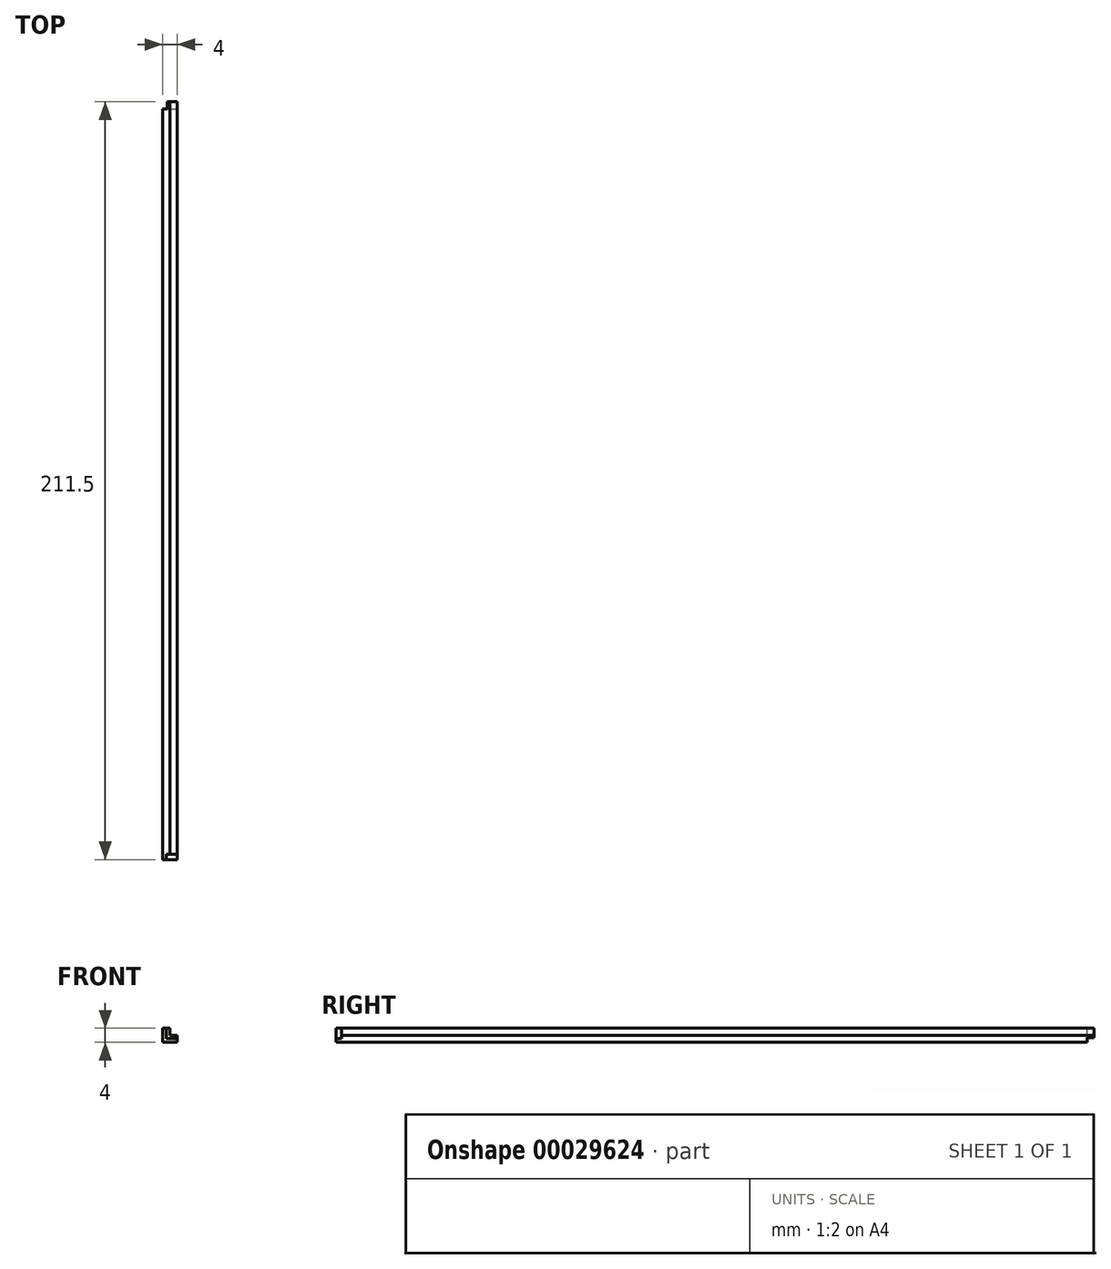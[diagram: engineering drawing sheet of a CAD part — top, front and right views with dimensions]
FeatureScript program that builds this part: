
annotation { "Feature Type Name" : "Feature", "Feature Type Description" : "" }
export const myFeature = defineFeature(function(context is Context, id is Id, definition is map)
    precondition{}
    {
        {
            var Q0;
            Q0=qCreatedBy(makeId("Top.planeOp"),FACE);
            var sketch = newSketch(context, id + "F0", { "sketchPlane" : qUnion([Q0])});
            skLineSegment(sketch, "E0.bottom", {"start": v(12.95, -61.2) * mm, "end": v(16.95, -61.2) * mm});
            skLineSegment(sketch, "E0.top", {"start": v(12.95, 148.8) * mm, "end": v(16.95, 148.8) * mm});
            skLineSegment(sketch, "E0.left", {"start": v(12.95, -61.2) * mm, "end": v(12.95, 148.8) * mm});
            skLineSegment(sketch, "E0.right", {"start": v(16.95, -61.2) * mm, "end": v(16.95, 148.8) * mm});
            skSolve(sketch);
        }
        {
            var Q0;
            Q0=makeQuery(id+"F0.imprint","IMPRINT",FACE,{"disambiguationData":[TD([[makeQuery(id+"F0.imprint","IMPRINT",EDGE,{"derivedFrom":sQuery(id+"F0.wireOp",EDGE,"E0.bottom")}),1.0]])]});
            extrude(context, id + "F1", {"entities" : qUnion([Q0]), "depth" : 2 * mm});
        }
        {
            var Q0;
            Q0=makeQuery(id+"F1.opExtrude","CAP_FACE",FACE,{"disambiguationData":[OSD([sQuery(id+"F0.wireOp",EDGE,"E0.bottom"),sQuery(id+"F0.wireOp",EDGE,"E0.top"),sQuery(id+"F0.wireOp",EDGE,"E0.left"),sQuery(id+"F0.wireOp",EDGE,"E0.right")])],"isStart":false});
            var sketch = newSketch(context, id + "F2", { "sketchPlane" : qUnion([Q0])});
            skLineSegment(sketch, "E1.bottom", {"start": v(12.95, -61.2) * mm, "end": v(14.95, -61.2) * mm});
            skLineSegment(sketch, "E1.left", {"start": v(12.95, -61.2) * mm, "end": v(12.95, 148.8) * mm});
            skLineSegment(sketch, "E2", {"start": v(14.95, -61.2) * mm, "end": v(14.95, 148.8) * mm});
            skLineSegment(sketch, "E3", {"start": v(14.95, 148.8) * mm, "end": v(12.95, 148.8) * mm});
            skSolve(sketch);
        }
        {
            var Q0;
            Q0=makeQuery(id+"F2.imprint","IMPRINT",FACE,{"disambiguationData":[TD([[makeQuery(id+"F2.imprint","IMPRINT",EDGE,{"derivedFrom":sQuery(id+"F2.wireOp",EDGE,"E1.bottom")}),1.0]])]});
            extrude(context, id + "F3", {"entities" : qUnion([Q0]), "operationType" : NewBodyOperationType.ADD, "depth" : 2 * mm});
        }
        {
            var Q0;
            Q0=makeQuery(id+"F3.boolean.opBoolean","MERGE",FACE,{"derivedFrom":[makeQuery(id+"F1.opExtrude","SWEPT_FACE",FACE,{"disambiguationData":[OSD([sQuery(id+"F0.wireOp",EDGE,"E0.top")])]}),makeQuery(id+"F3.opExtrude","SWEPT_FACE",FACE,{"disambiguationData":[OSD([sQuery(id+"F2.wireOp",EDGE,"E3")])]})]});
            var sketch = newSketch(context, id + "F4", { "sketchPlane" : qUnion([Q0])});
            skLineSegment(sketch, "E4", {"start": v(-12.95, 4) * mm, "end": v(-12.95, 0) * mm});
            skLineSegment(sketch, "E5", {"start": v(-12.95, 0) * mm, "end": v(-16.95, 0) * mm});
            skLineSegment(sketch, "E6", {"start": v(-16.95, 0) * mm, "end": v(-16.95, 1.3) * mm});
            skLineSegment(sketch, "E7", {"start": v(-14.25, 1.3) * mm, "end": v(-14.25, 4) * mm});
            skLineSegment(sketch, "E8", {"start": v(-14.25, 4) * mm, "end": v(-12.95, 4) * mm});
            skLineSegment(sketch, "E9", {"start": v(-14.25, 1.3) * mm, "end": v(-16.95, 1.3) * mm});
            skPoint(sketch, "E10.orphan", {"position": v(-16.95, 1) * mm});
            skSolve(sketch);
        }
        {
            var Q0;
            Q0 = qSketchRegion(id + "F4", true);
            extrude(context, id + "F5", {"entities" : qUnion([Q0]), "operationType" : NewBodyOperationType.REMOVE, "oppositeDirection" : true, "depth" : 2 * mm});
        }
        {
            var Q0;
            Q0=makeQuery(id+"F3.boolean.opBoolean","MERGE",FACE,{"derivedFrom":[makeQuery(id+"F1.opExtrude","SWEPT_FACE",FACE,{"disambiguationData":[OSD([sQuery(id+"F0.wireOp",EDGE,"E0.bottom")])]}),makeQuery(id+"F3.opExtrude","SWEPT_FACE",FACE,{"disambiguationData":[OSD([sQuery(id+"F2.wireOp",EDGE,"E1.bottom")])]})]});
            var sketch = newSketch(context, id + "F6", { "sketchPlane" : qUnion([Q0])});
            skLineSegment(sketch, "E11", {"start": v(12.95, 4) * mm, "end": v(12.95, 0) * mm});
            skLineSegment(sketch, "E12", {"start": v(12.95, 0) * mm, "end": v(16.95, 0) * mm});
            skLineSegment(sketch, "E13", {"start": v(16.95, 0) * mm, "end": v(16.95, 1) * mm});
            skLineSegment(sketch, "E14", {"start": v(16.95, 1) * mm, "end": v(13.95, 1) * mm});
            skLineSegment(sketch, "E15", {"start": v(13.95, 1) * mm, "end": v(13.95, 4) * mm});
            skLineSegment(sketch, "E16", {"start": v(13.95, 4) * mm, "end": v(12.95, 4) * mm});
            skSolve(sketch);
        }
        {
            var Q0;
            Q0=makeQuery(id+"F6.imprint","IMPRINT",FACE,{"disambiguationData":[TD([[makeQuery(id+"F6.imprint","IMPRINT",EDGE,{"derivedFrom":sQuery(id+"F6.wireOp",EDGE,"E11")}),1.0]])]});
            extrude(context, id + "F7", {"entities" : qUnion([Q0]), "operationType" : NewBodyOperationType.ADD, "depth" : 1.5 * mm});
        }
    });
